# Revit family: Inbox Booths_Tuesday
name_source: partatom
category: Furniture
units: mm (PartAtom-declared; Revit-internal decimal feet)

## family parameters
Always vertical = Yes
Cut with Voids When Loaded = Yes
Enable Cutting in Views = No
OmniClass Number = 23.40.20.00
OmniClass Title = General Furniture and Specialties
Render Appearance Source = Family Geometry
Room Calculation Point = No
Shared = Yes
Work Plane-Based = No

## types (1)
- Inbox Booths_Tuesday
    BB_Carpet = Default
    BB_Door Swing = Yes
    BB_Frame = Default
    BB_Furniture = Default
    BB_Glass Panel = Glass
    BB_Handle = Default
    BB_Interior Panel 01 = Default
    BB_Internal Panel 02 = Default
    BB_Lamp = Default
    BB_Light Source = Default Light Source
    BB_Set Out Lines = Yes
    BB_Table = Default
    BIM Content Publish Revit Version = Revit 2024.1
    DEPTH (DO NOT EDIT) = 900 mm
    Default Elevation = 0 mm  [stored 0 ft]
    Description = Small portable focus booth which offers individual users confidential and private working spaces
    HEIGHT (DO NOT EDIT) = 2100 mm
    Manufacturer = Inbox Booths
    Model = Small Focus Pod
    OwnedBy = Inbox Furniture
    URL = https://inboxbooths.com
    WIDTH (DO NOT EDIT) = 1100 mm

note: [stored X ft] marks values corroborated as IEEE doubles in the binary element streams (Revit-internal decimal feet)

## geometry (parser evidence)
native form markers: Sweep x3
no freeform markers — native parametric forms only
